# Revit family: DONNA WALL
name_source: partatom
category: Lighting Fixtures
units: mm (PartAtom-declared; Revit-internal decimal feet)

## family parameters
Cut with Voids When Loaded = No
Host = Face
Light Source = Yes
Part Type = Normal
Room Calculation Point = No
Round Connector Dimension = Use Diameter
Shared = No

## types (4) — shared parameters
AssetType = Fixed installation
Brand = Pholc
Category = Wall lamp
Class = Class 1
Color Filter = 16777215
Default Elevation = 1700 mm  [stored 5.57743 ft]
Dimming Lamp Color Temperature Shift = <None>
ElectricalDeviceNominalPower = 10
Emit from Line Length = 5 mm  [stored 0.0164042 ft]
Features = Include lightsource in the box
IFC classification = Light Fixture
IP_Code = IP20
Lamp = LED
Light Source Symbol Length = 200 mm  [stored 0.656168 ft]
LightFixtureMountingType = SURFACE
LightFixturePlacingType = WALL
Lightsource included = Yes
Lightsource type = LED
Manufacturer = Pholc
ManufacturerName = Pholc
ManufacturerURL = https://www.pholc.se
Model = Donna wall
NBS Reference Description = General Lighting Systems
NBSReference = 70-80-33
Name = Donna wall
Nominal Length = 65 mm
NominalCurrent = 0 A
NominalVoltage = 0 V
Shape = Sculptured
Size = 15x7,6x6,5
Socket = GU10
Spot Beam Angle = 60.00°
Spot Field Angle = 60.00°
Tilt Angle = 90.00°
TotalWattage = 10 W
URL = https://www.pholc.se
Uniclass2015Description = Surface luminaires
Uniclass2015Reference = Pr_70_70_48_85
Wattage Comments = 10

## per-type parameters (varying)
| type | ArticleNumber | Color | Material | Material Outer | ModelNumber | Nominal Height | Nominal Width | VisualHusRef |
| Donna wall - Linen | 960213 | NCS S 1005-Y | NCS S 1005-Y | Linen (NCS S 1005-Y) | 960213 | 150 mm | 76 mm  [stored 0.249344 ft] | Pholc_Id077 |
| Donna wall - Blush | 960214 | NCS S 4020-Y20R | NCS S 4020-Y20R | Blush (NCS S 4020-Y20R) | 960214 | 1219 mm | 0 mm  [stored 0 ft] |  |
| Donna wall - Black inc | 960215 | NCS S 7502-B | NCS S 7502-B | Black inc (NCS S 7502-B) | 960215 | 1219 mm | 0 mm  [stored 0 ft] |  |
| Donna wall - Autumn leaves | 960218 | NCS S 3030-Y10R | NCS S 3030-Y10R | Autumn leaves (NCS S 3030-Y10R) | 960218 | 1219 mm | 0 mm  [stored 0 ft] |  |

note: [stored X ft] marks values corroborated as IEEE doubles in the binary element streams (Revit-internal decimal feet)

## geometry (parser evidence)
native form markers: Sweep x3
no freeform markers — native parametric forms only
